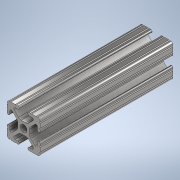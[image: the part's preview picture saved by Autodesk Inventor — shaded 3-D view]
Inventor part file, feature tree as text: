
AUTODESK INVENTOR PART (.ipt)
format: ipt  version: 2020 (Build 240168000, 168)  size: 241,664 bytes
history: native  units: in
note: dims shown in document units (in); Inventor stores cm internally (conversion verified against a paired STEP export)
features: extrude x1, sketch x1
ambient origin geometry x8: Origin, YZ Plane, XZ Plane, XY Plane, X Axis, Y Axis, Z Axis, Center Point
bodies: Solid1 (feature_tree)
feature tree (2):
  extrude  "Extrusion1"  [1 undecoded]
  sketch  "Sketch1"  dims[d0=4.0in d1=0.0in]
note: 1 required parameter value undecoded (feature->parameter linkage not recoverable at this tier; creation-order binding heuristic only, values carry confidence <= 0.55)
